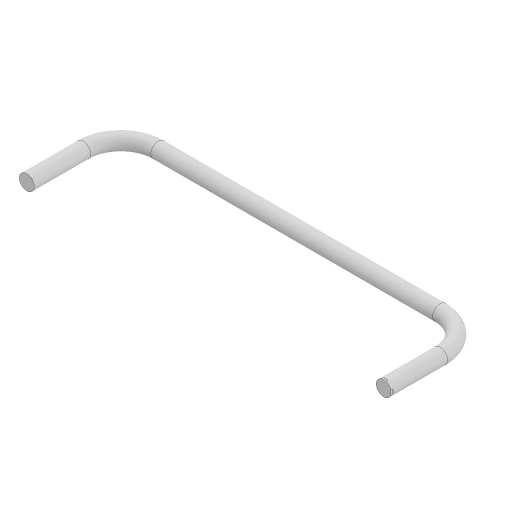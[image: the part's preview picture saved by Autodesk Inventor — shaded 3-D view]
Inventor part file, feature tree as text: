
AUTODESK INVENTOR PART (.ipt)
format: ipt  version: 2024.3 (Build 283343000, 343)  size: 126,464 bytes
history: native  units: mm
features: sketch x4, extrude x3, mirror x2, projected_geometry x2, revolve x1
ambient origin geometry x8: Origin, YZ Plane, XZ Plane, XY Plane, X Axis, Y Axis, Z Axis, Center Point
bodies: Solid1 (feature_tree)
feature tree (12):
  extrude  "Extrusion1"  Depth=150.0mm TaperAngle=0.0deg
  revolve  "Revolution1"  [1 undecoded]
  mirror  "Mirror1"
  extrude  "Extrusion3"  Depth=30.0mm TaperAngle=0.0deg
  mirror  "Mirror2"
  extrude  "Extrusion4"  Depth=1.0mm
  sketch  "Sketch1"  dims[d0=8.0mm d1=150.0mm d2=0.0mm]
  sketch  "Sketch4"  dims[d9=90.0deg d10=20.0mm]
  sketch  "Sketch5"  dims[d11=0.0mm d12=30.0mm d13=0.0mm]
  projected_geometry  "Projected Loop2"
  sketch  "Sketch6"  dims[d14=1.0mm d15=0.0mm d7=0.5mm d8=0.872665mm]
  projected_geometry  "Projected Loop3"
note: 1 required parameter value undecoded (feature->parameter linkage not recoverable at this tier; creation-order binding heuristic only, values carry confidence <= 0.55)
